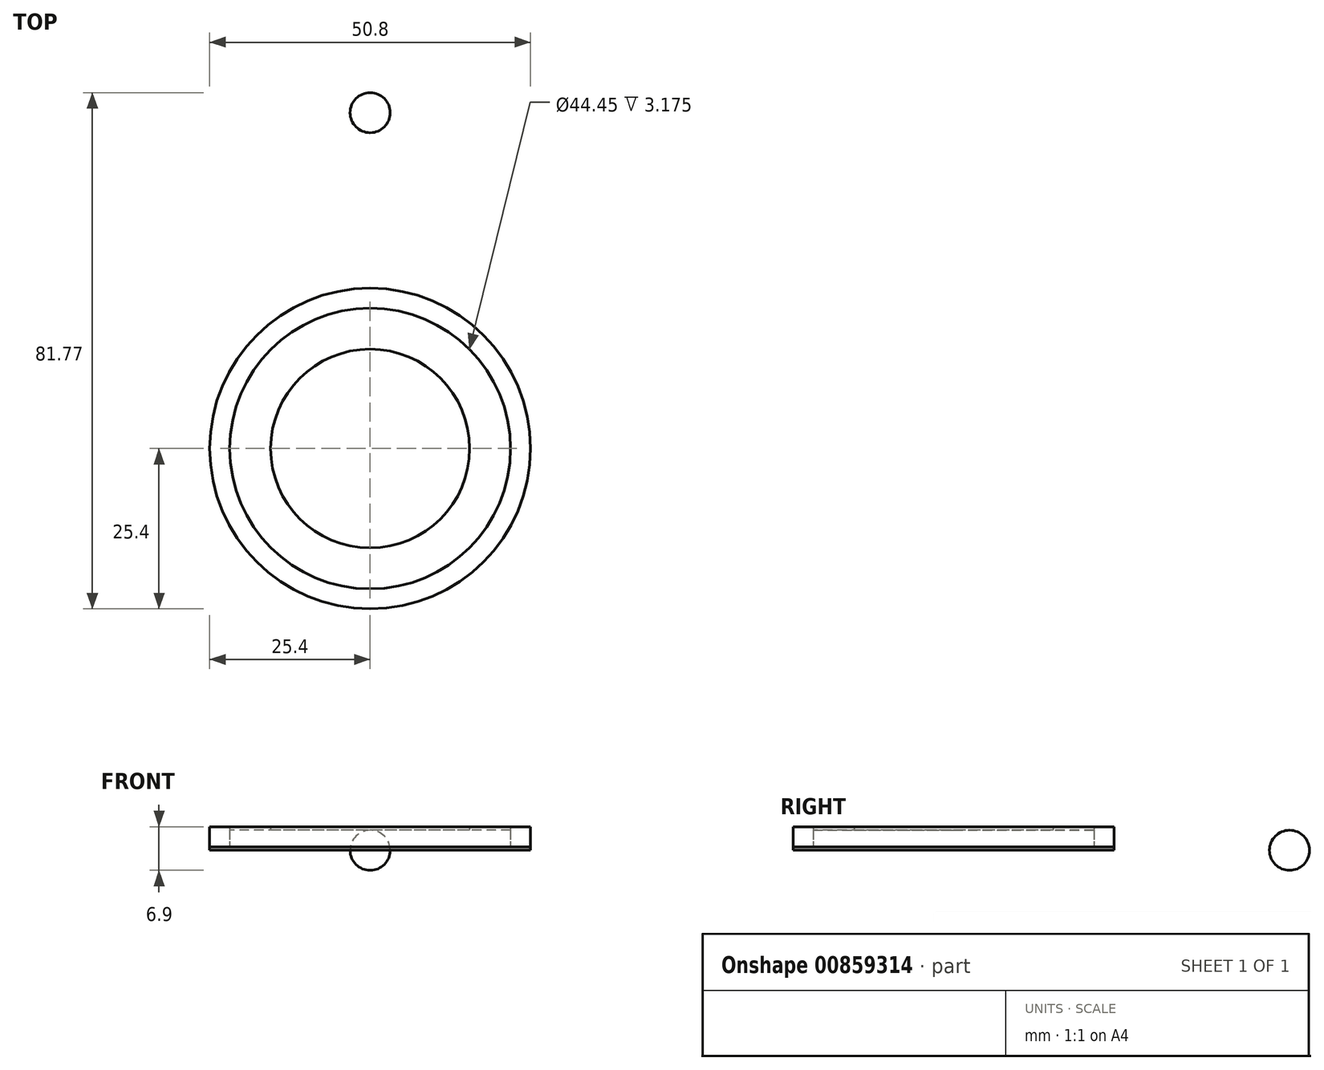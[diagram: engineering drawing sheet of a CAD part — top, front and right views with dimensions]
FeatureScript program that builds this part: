
annotation { "Feature Type Name" : "Feature", "Feature Type Description" : "" }
export const myFeature = defineFeature(function(context is Context, id is Id, definition is map)
    precondition{}
    {
        {
            assignVariable(context, id + "F0", {"name" : "width", "anyValue" : .55});
        }
        {
            var Q0;
            Q0=qCreatedBy(makeId("Top.planeOp"),FACE);
            var sketch = newSketch(context, id + "F1", { "sketchPlane" : qUnion([Q0])});
            skCircle(sketch, "E0", {"center": v(0, 0) * mm, "radius": 25.4 * mm});
            skCircle(sketch, "E1", {"center": v(0, 0) * mm, "radius": 22.23 * mm});
            skCircle(sketch, "E2", {"center": v(0, 0) * mm, "radius": 15.75 * mm});
            skSolve(sketch);
        }
        {
            var Q0;
            Q0=makeQuery(id+"F1.imprint","IMPRINT",FACE,{"disambiguationData":[TD([[makeQuery(id+"F1.imprint","IMPRINT",EDGE,{"derivedFrom":sQuery(id+"F1.wireOp",EDGE,"E0")}),1.0]])]});
            extrude(context, id + "F2", {"entities" : qUnion([Q0]), "depth" : (getVariable(context, 'width')) * mm, "offsetDistance" : 25.4 * mm});
        }
        {
            var Q0;
            Q0=makeQuery(id+"F1.imprint","IMPRINT",FACE,{"disambiguationData":[TD([[makeQuery(id+"F1.imprint","IMPRINT",EDGE,{"derivedFrom":sQuery(id+"F1.wireOp",EDGE,"E2")}),1.0]])]});
            extrude(context, id + "F3", {"entities" : qUnion([Q0]), "depth" : (getVariable(context, 'width')) * mm, "offsetDistance" : 25.4 * mm});
        }
        {
            var Q0;
            Q0=qCreatedBy(makeId("Top.planeOp"),FACE);
            var sketch = newSketch(context, id + "F4", { "sketchPlane" : qUnion([Q0])});
            skArc(sketch, "E3", {"start": v(0, 56.37) * mm, "mid": v(-3.18, 53.2) * mm, "end": v(0, 50.02) * mm});
            skLineSegment(sketch, "E4", {"start": v(0, 56.37) * mm, "end": v(0, 50.02) * mm});
            skSolve(sketch);
        }
        {
            var Q0;
            Q0=makeQuery(id+"F4.imprint","IMPRINT",FACE,{"disambiguationData":[TD([[makeQuery(id+"F4.imprint","IMPRINT",EDGE,{"derivedFrom":sQuery(id+"F4.wireOp",EDGE,"E3")}),1.0]])]});
            var Q1;
            Q1=sQuery(id+"F4.wireOp",EDGE,"E4");
            revolve(context, id + "F5", {"surfaceOperationType" : NewSurfaceOperationType.NEW, "entities" : qUnion([Q0]), "axis" : qUnion([Q1]), "revolveType" : RevolveType.FULL});
        }
        {
            var Q0;
            Q0=makeQuery(id+"F1.imprint","IMPRINT",FACE,{"disambiguationData":[TD([[makeQuery(id+"F1.imprint","IMPRINT",EDGE,{"derivedFrom":sQuery(id+"F1.wireOp",EDGE,"E1")}),1.0]])]});
            extrude(context, id + "F6", {"entities" : qUnion([Q0]), "operationType" : NewBodyOperationType.ADD, "depth" : 3.17 * mm, "offsetDistance" : 25.4 * mm});
        }
        {
            var Q0;
            Q0=makeQuery(id+"F2.opExtrude","CAP_FACE",FACE,{"disambiguationData":[OSD([sQuery(id+"F1.wireOp",EDGE,"E0"),sQuery(id+"F1.wireOp",EDGE,"E1")])],"isStart":false});
            var sketch = newSketch(context, id + "F7", { "sketchPlane" : qUnion([Q0])});
            skCircle(sketch, "E5", {"center": v(0, 0) * mm, "radius": 28.58 * mm});
            skSolve(sketch);
        }
        {
            var Q0;
            Q0=makeQuery(id+"F7.imprint","IMPRINT",FACE,{"disambiguationData":[TD([[makeQuery(id+"F7.imprint","IMPRINT",EDGE,{"derivedFrom":makeQuery(id+"F2.opExtrude","CAP_EDGE",EDGE,{"disambiguationData":[OSD([sQuery(id+"F1.wireOp",EDGE,"E0")])],"isStart":false})}),1.0]])]});
            var Q1;
            Q1=makeQuery(id+"F7.imprint","IMPRINT",FACE,{"disambiguationData":[TD([[makeQuery(id+"F7.imprint","IMPRINT",EDGE,{"derivedFrom":makeQuery(id+"F2.opExtrude","CAP_EDGE",EDGE,{"disambiguationData":[OSD([sQuery(id+"F1.wireOp",EDGE,"E1")])],"isStart":false})}),1.0]])]});
            extrude(context, id + "F8", {"entities" : qUnion([Q0, Q1]), "depth" : 3.17 * mm, "offsetDistance" : 25.4 * mm});
        }
        {
            var Q0;
            Q0=makeQuery(id+"F3.opExtrude","CAP_FACE",FACE,{"disambiguationData":[OSD([sQuery(id+"F1.wireOp",EDGE,"E2")])],"isStart":false});
            extrude(context, id + "F9", {"entities" : qUnion([Q0]), "operationType" : NewBodyOperationType.REMOVE, "depth" : 52.32 * mm, "offsetDistance" : 25.4 * mm});
        }
        {
            var Q0;
            Q0=makeQuery(id+"F3.opExtrude","CAP_FACE",FACE,{"disambiguationData":[OSD([sQuery(id+"F1.wireOp",EDGE,"E2")])],"isStart":false});
            extrude(context, id + "F10", {"entities" : qUnion([Q0]), "operationType" : NewBodyOperationType.ADD, "depth" : 3.17 * mm, "offsetDistance" : 25.4 * mm});
        }
    });
